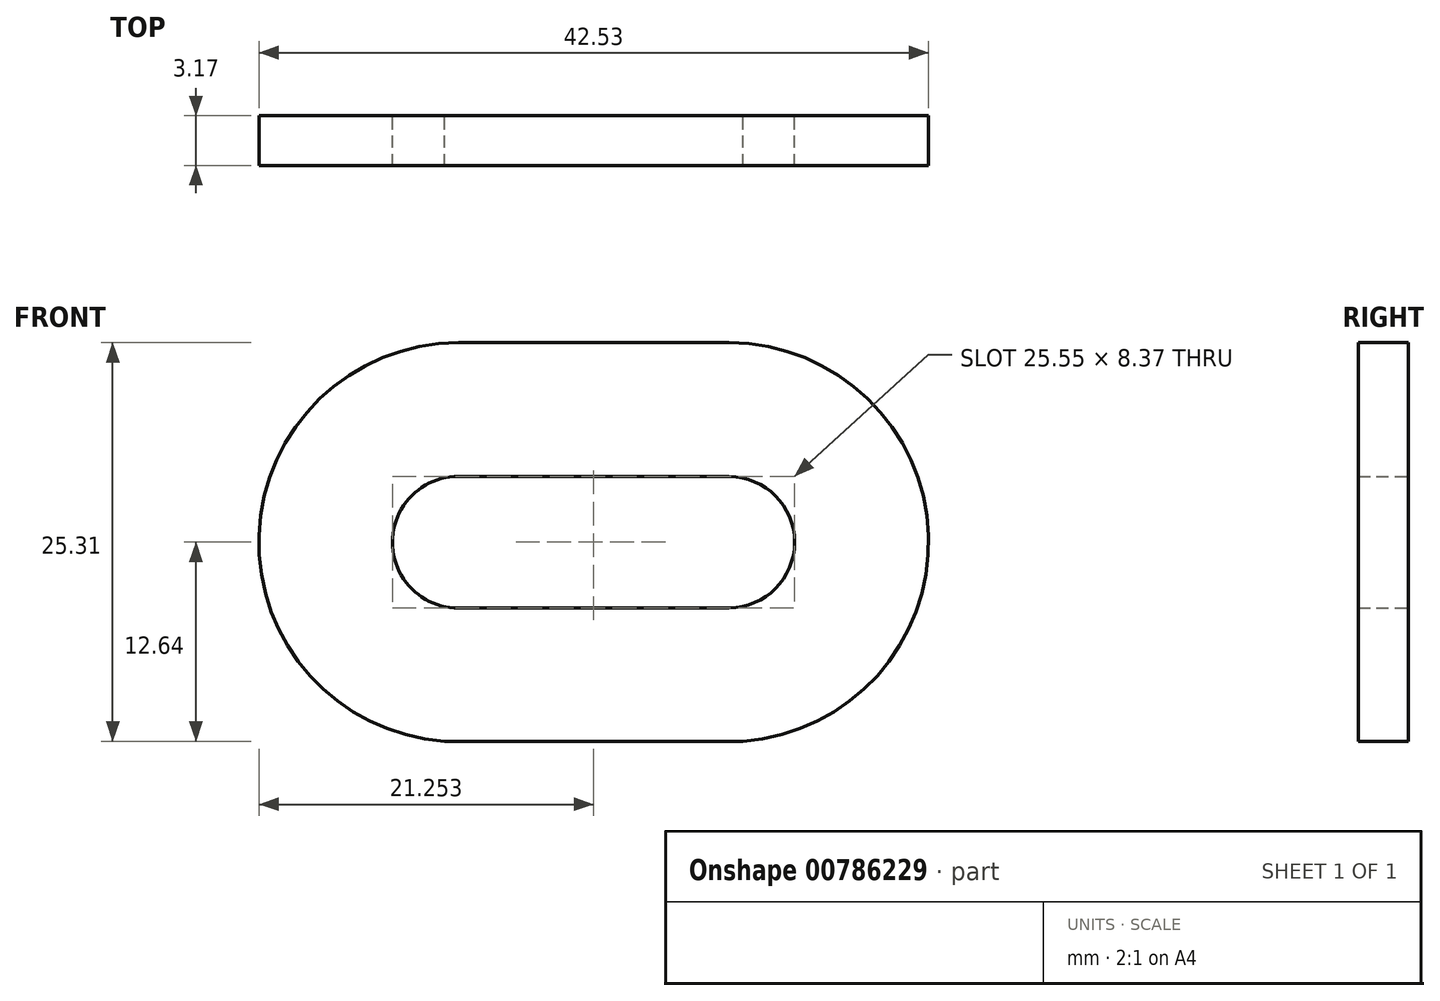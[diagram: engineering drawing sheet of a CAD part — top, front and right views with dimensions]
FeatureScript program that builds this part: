
annotation { "Feature Type Name" : "Feature", "Feature Type Description" : "" }
export const myFeature = defineFeature(function(context is Context, id is Id, definition is map)
    precondition{}
    {
        {
            var Q0;
            Q0=qCreatedBy(makeId("Front.planeOp"),FACE);
            var sketch = newSketch(context, id + "F0", { "sketchPlane" : qUnion([Q0])});
            skArc(sketch, "E0", {"start": v(-9.1, 4.19) * mm, "mid": v(-13.3, 0) * mm, "end": v(-9.1, -4.19) * mm});
            skArc(sketch, "E1", {"start": v(8.96, -12.64) * mm, "mid": v(20.75, 0.44) * mm, "end": v(8.08, 12.67) * mm});
            skArc(sketch, "E2", {"start": v(8.09, -4.16) * mm, "mid": v(12.25, 0) * mm, "end": v(8.09, 4.16) * mm});
            skLineSegment(sketch, "E3", {"start": v(-9.11, 12.67) * mm, "end": v(8.08, 12.67) * mm});
            skLineSegment(sketch, "E4", {"start": v(-10, -12.64) * mm, "end": v(8.96, -12.64) * mm});
            skLineSegment(sketch, "E5", {"start": v(-9.1, 4.19) * mm, "end": v(8.09, 4.16) * mm});
            skLineSegment(sketch, "E6", {"start": v(-9.1, -4.19) * mm, "end": v(8.09, -4.16) * mm});
            skArc(sketch, "E7.trimOffspring", {"start": v(-9.11, 12.67) * mm, "mid": v(-21.78, 0.44) * mm, "end": v(-10, -12.64) * mm});
            skSolve(sketch);
        }
        {
            var Q0;
            Q0 = qSketchRegion(id + "F0", true);
            extrude(context, id + "F1", {"entities" : qUnion([Q0]), "depth" : 3.17 * mm, "offsetDistance" : 25.4 * mm});
        }
    });
